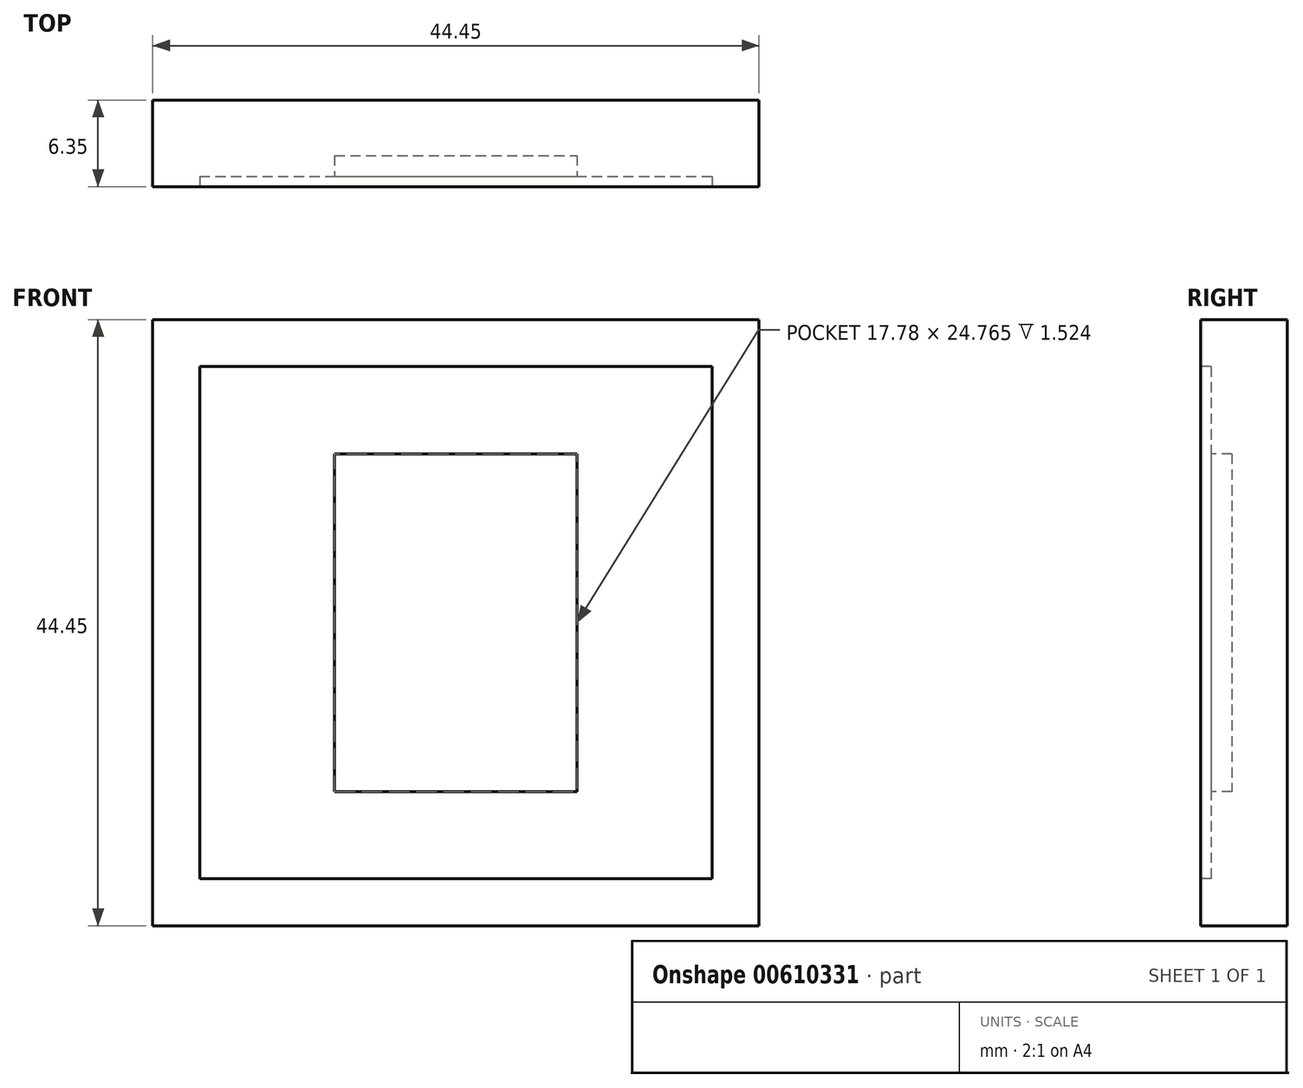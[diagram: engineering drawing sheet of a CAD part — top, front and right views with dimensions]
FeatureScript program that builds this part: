
annotation { "Feature Type Name" : "Feature", "Feature Type Description" : "" }
export const myFeature = defineFeature(function(context is Context, id is Id, definition is map)
    precondition{}
    {
        {
            var Q0;
            Q0=qCreatedBy(makeId("Front.planeOp"),FACE);
            var sketch = newSketch(context, id + "F0", { "sketchPlane" : qUnion([Q0])});
            skLineSegment(sketch, "E0.bottom", {"start": v(0, 0) * mm, "end": v(44.45, 0) * mm});
            skLineSegment(sketch, "E0.top", {"start": v(0, -44.45) * mm, "end": v(44.45, -44.45) * mm});
            skLineSegment(sketch, "E0.left", {"start": v(0, 0) * mm, "end": v(0, -44.45) * mm});
            skLineSegment(sketch, "E0.right", {"start": v(44.45, 0) * mm, "end": v(44.45, -44.45) * mm});
            skSolve(sketch);
        }
        {
            var Q0;
            Q0 = qSketchRegion(id + "F0", true);
            extrude(context, id + "F1", {"entities" : qUnion([Q0]), "depth" : 6.35 * mm, "offsetDistance" : 25.4 * mm});
        }
        {
            var Q0;
            Q0=makeQuery(id+"F1.opExtrude","CAP_FACE",FACE,{"disambiguationData":[OSD([sQuery(id+"F0.wireOp",EDGE,"E0.bottom"),sQuery(id+"F0.wireOp",EDGE,"E0.top"),sQuery(id+"F0.wireOp",EDGE,"E0.left"),sQuery(id+"F0.wireOp",EDGE,"E0.right")])],"isStart":false});
            var sketch = newSketch(context, id + "F2", { "sketchPlane" : qUnion([Q0])});
            skLineSegment(sketch, "E1.bottom", {"start": v(3.44, -3.44) * mm, "end": v(41, -3.44) * mm});
            skLineSegment(sketch, "E1.top", {"start": v(3.44, -41) * mm, "end": v(41, -41) * mm});
            skLineSegment(sketch, "E1.left", {"start": v(3.44, -3.44) * mm, "end": v(3.44, -41) * mm});
            skLineSegment(sketch, "E1.right", {"start": v(41, -3.44) * mm, "end": v(41, -41) * mm});
            skPoint(sketch, "E1.middle", {"position": v(22.23, -22.22) * mm});
            skPoint(sketch, "E1.middle.positionSnap0", {"position": v(22.23, 0) * mm});
            skPoint(sketch, "E1.middle.positionSnap1", {"position": v(0, -22.23) * mm});
            skPoint(sketch, "E1.centerSnap0", {"position": v(22.23, 0) * mm});
            skPoint(sketch, "E1.centerSnap1", {"position": v(0, -22.23) * mm});
            skPoint(sketch, "E2.center.orphan", {"position": v(3.44, -3.44) * mm});
            skPoint(sketch, "E3.second.point", {"position": v(3.44, -4.15) * mm});
            skPoint(sketch, "E3.third.point", {"position": v(3.3, -3.21) * mm});
            skPoint(sketch, "E4.orphan", {"position": v(3.44, -4.24) * mm});
            skSolve(sketch);
        }
        {
            var Q0;
            Q0 = qSketchRegion(id + "F2", true);
            extrude(context, id + "F3", {"entities" : qUnion([Q0]), "operationType" : NewBodyOperationType.REMOVE, "oppositeDirection" : true, "depth" : 0.76 * mm, "offsetDistance" : 25.4 * mm});
        }
        {
            var Q0;
            Q0=makeQuery(id+"F3.boolean.opBoolean","COPY",FACE,{"derivedFrom":makeQuery(id+"F3.opExtrude","CAP_FACE",FACE,{"disambiguationData":[OSD([sQuery(id+"F2.wireOp",EDGE,"E1.bottom"),sQuery(id+"F2.wireOp",EDGE,"E1.top"),sQuery(id+"F2.wireOp",EDGE,"E1.left"),sQuery(id+"F2.wireOp",EDGE,"E1.right")])],"isStart":false})});
            var sketch = newSketch(context, id + "F4", { "sketchPlane" : qUnion([Q0])});
            skLineSegment(sketch, "E5.bottom", {"start": v(13.34, -9.84) * mm, "end": v(31.12, -9.84) * mm});
            skLineSegment(sketch, "E5.top", {"start": v(13.34, -34.6) * mm, "end": v(31.12, -34.6) * mm});
            skLineSegment(sketch, "E5.left", {"start": v(13.34, -9.84) * mm, "end": v(13.34, -34.6) * mm});
            skLineSegment(sketch, "E5.right", {"start": v(31.12, -9.84) * mm, "end": v(31.12, -34.6) * mm});
            skPoint(sketch, "E5.middle", {"position": v(22.23, -22.22) * mm});
            skPoint(sketch, "E5.middle.positionSnap0", {"position": v(22.23, -3.44) * mm});
            skPoint(sketch, "E5.middle.positionSnap1", {"position": v(3.44, -22.22) * mm});
            skPoint(sketch, "E5.centerSnap0", {"position": v(22.23, -3.44) * mm});
            skPoint(sketch, "E5.centerSnap1", {"position": v(3.44, -22.22) * mm});
            skSolve(sketch);
        }
        {
            var Q0;
            Q0 = qSketchRegion(id + "F4", true);
            extrude(context, id + "F5", {"entities" : qUnion([Q0]), "operationType" : NewBodyOperationType.REMOVE, "oppositeDirection" : true, "depth" : 1.52 * mm, "offsetDistance" : 25.4 * mm});
        }
    });
